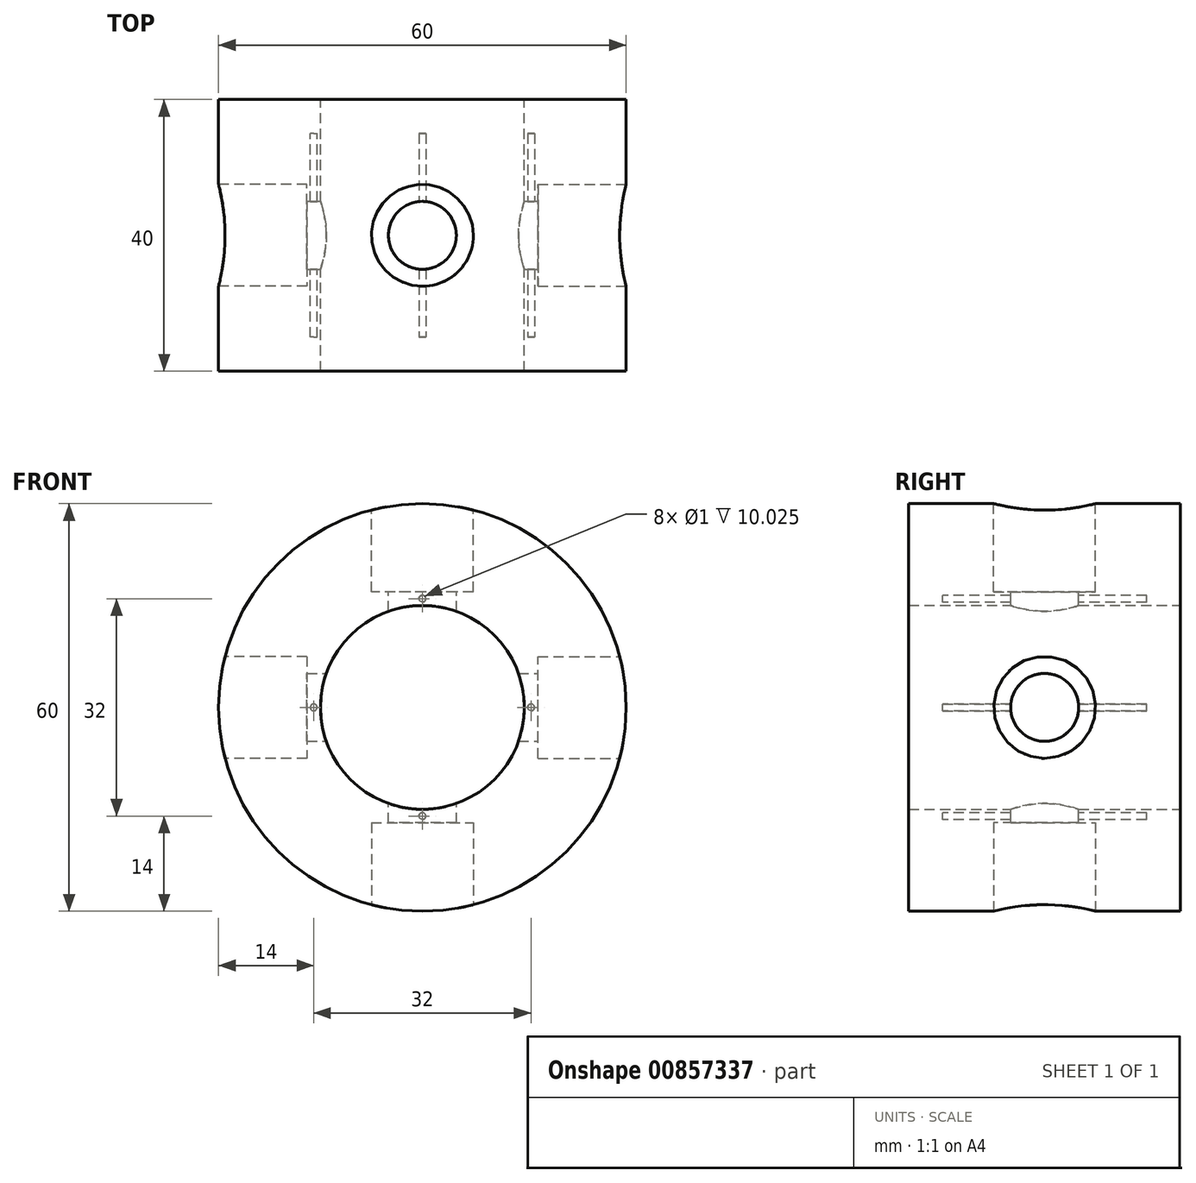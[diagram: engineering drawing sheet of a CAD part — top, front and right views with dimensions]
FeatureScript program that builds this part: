
annotation { "Feature Type Name" : "Feature", "Feature Type Description" : "" }
export const myFeature = defineFeature(function(context is Context, id is Id, definition is map)
    precondition{}
    {
        {
            var Q0;
            Q0=qCreatedBy(makeId("Front.planeOp"),FACE);
            var sketch = newSketch(context, id + "F0", { "sketchPlane" : qUnion([Q0])});
            skCircle(sketch, "E0", {"center": v(0, 0) * mm, "radius": 30 * mm});
            skCircle(sketch, "E1", {"center": v(0, 0) * mm, "radius": 15 * mm});
            skSolve(sketch);
        }
        {
            var Q0;
            Q0=makeQuery(id+"F0.imprint","IMPRINT",FACE,{"disambiguationData":[TD([[makeQuery(id+"F0.imprint","IMPRINT",EDGE,{"derivedFrom":sQuery(id+"F0.wireOp",EDGE,"E0")}),1.0]])]});
            extrude(context, id + "F1", {"entities" : qUnion([Q0]), "endBound" : BoundingType.SYMMETRIC, "depth" : 40 * mm, "offsetDistance" : 25 * mm});
        }
        {
            var Q0;
            Q0=qCreatedBy(makeId("Top.planeOp"),FACE);
            cPlane(context, id + "F2", {"entities" : qUnion([Q0]), "cplaneType" : CPlaneType.OFFSET, "offset" : 30 * mm, "width" : 150 * mm, "height" : 150 * mm});
        }
        {
            var Q0;
            Q0=qCreatedBy(id+"F2.planeOp",FACE);
            var sketch = newSketch(context, id + "F3", { "sketchPlane" : qUnion([Q0])});
            skCircle(sketch, "E2", {"center": v(0, 0) * mm, "radius": 7.5 * mm});
            skSolve(sketch);
        }
        {
            var Q0;
            Q0 = qSketchRegion(id + "F3", true);
            extrude(context, id + "F4", {"entities" : qUnion([Q0]), "operationType" : NewBodyOperationType.REMOVE, "oppositeDirection" : true, "depth" : 13 * mm, "offsetDistance" : 25 * mm});
        }
        {
            var Q0;
            Q0=qCreatedBy(id+"F2.planeOp",FACE);
            var sketch = newSketch(context, id + "F5", { "sketchPlane" : qUnion([Q0])});
            skCircle(sketch, "E3", {"center": v(0, 0) * mm, "radius": 5 * mm});
            skSolve(sketch);
        }
        {
            var Q0;
            Q0 = qSketchRegion(id + "F5", true);
            extrude(context, id + "F6", {"entities" : qUnion([Q0]), "operationType" : NewBodyOperationType.REMOVE, "oppositeDirection" : true, "depth" : 65.5 * mm, "offsetDistance" : 25 * mm});
        }
        {
            var Q0;
            Q0=qCreatedBy(makeId("Top.planeOp"),FACE);
            cPlane(context, id + "F7", {"entities" : qUnion([Q0]), "cplaneType" : CPlaneType.OFFSET, "offset" : 30 * mm, "oppositeDirection" : true, "width" : 150 * mm, "height" : 150 * mm});
        }
        {
            var Q0;
            Q0=qCreatedBy(id+"F7.planeOp",FACE);
            var sketch = newSketch(context, id + "F8", { "sketchPlane" : qUnion([Q0])});
            skCircle(sketch, "E4", {"center": v(0, 0) * mm, "radius": 7.5 * mm});
            skSolve(sketch);
        }
        {
            var Q0;
            Q0 = qSketchRegion(id + "F8", true);
            extrude(context, id + "F9", {"entities" : qUnion([Q0]), "operationType" : NewBodyOperationType.REMOVE, "depth" : 13 * mm, "offsetDistance" : 25 * mm});
        }
        {
            var Q0;
            Q0=qCreatedBy(makeId("Right.planeOp"),FACE);
            cPlane(context, id + "F10", {"entities" : qUnion([Q0]), "cplaneType" : CPlaneType.OFFSET, "offset" : 30 * mm, "width" : 150 * mm, "height" : 150 * mm});
        }
        {
            var Q0;
            Q0=qCreatedBy(makeId("Right.planeOp"),FACE);
            cPlane(context, id + "F11", {"entities" : qUnion([Q0]), "cplaneType" : CPlaneType.OFFSET, "offset" : 30 * mm, "oppositeDirection" : true, "width" : 150 * mm, "height" : 150 * mm});
        }
        {
            var Q0;
            Q0=qCreatedBy(id+"F10.planeOp",FACE);
            var sketch = newSketch(context, id + "F12", { "sketchPlane" : qUnion([Q0])});
            skCircle(sketch, "E5", {"center": v(0, 0) * mm, "radius": 7.5 * mm});
            skSolve(sketch);
        }
        {
            var Q0;
            Q0 = qSketchRegion(id + "F12", true);
            extrude(context, id + "F13", {"entities" : qUnion([Q0]), "operationType" : NewBodyOperationType.REMOVE, "oppositeDirection" : true, "depth" : 13 * mm, "offsetDistance" : 25 * mm});
        }
        {
            var Q0;
            Q0=qCreatedBy(id+"F10.planeOp",FACE);
            var sketch = newSketch(context, id + "F14", { "sketchPlane" : qUnion([Q0])});
            skCircle(sketch, "E6", {"center": v(0, 0) * mm, "radius": 5 * mm});
            skSolve(sketch);
        }
        {
            var Q0;
            Q0 = qSketchRegion(id + "F14", true);
            extrude(context, id + "F15", {"entities" : qUnion([Q0]), "operationType" : NewBodyOperationType.REMOVE, "oppositeDirection" : true, "depth" : 92 * mm, "offsetDistance" : 25 * mm});
        }
        {
            var Q0;
            Q0=qCreatedBy(id+"F11.planeOp",FACE);
            var sketch = newSketch(context, id + "F16", { "sketchPlane" : qUnion([Q0])});
            skCircle(sketch, "E7", {"center": v(0, 0) * mm, "radius": 7.5 * mm});
            skSolve(sketch);
        }
        {
            var Q0;
            Q0 = qSketchRegion(id + "F16", true);
            extrude(context, id + "F17", {"entities" : qUnion([Q0]), "operationType" : NewBodyOperationType.REMOVE, "depth" : 13 * mm, "offsetDistance" : 25 * mm});
        }
        {
            var Q0;
            Q0=qCreatedBy(makeId("Front.planeOp"),FACE);
            var sketch = newSketch(context, id + "F18", { "sketchPlane" : qUnion([Q0])});
            skLineSegment(sketch, "E8", {"start": v(0, 0) * mm, "end": v(0, 16) * mm});
            skCircle(sketch, "E9", {"center": v(0, 16) * mm, "radius": 0.5 * mm});
            skCircle(sketch, "E10.1.0", {"center": v(-16, 0) * mm, "radius": 0.5 * mm});
            skCircle(sketch, "E10.2.0", {"center": v(0, -16) * mm, "radius": 0.5 * mm});
            skCircle(sketch, "E10.3.0", {"center": v(16, 0) * mm, "radius": 0.5 * mm});
            skPoint(sketch, "E10.center", {"position": v(0, 0) * mm});
            skSolve(sketch);
        }
        {
            var Q0;
            Q0=makeQuery(id+"F18.imprint","IMPRINT",FACE,{"disambiguationData":[TD([[makeQuery(id+"F18.imprint","IMPRINT",EDGE,{"derivedFrom":sQuery(id+"F18.wireOp",EDGE,"E9")}),1.0]])]});
            extrude(context, id + "F19", {"entities" : qUnion([Q0]), "operationType" : NewBodyOperationType.REMOVE, "endBound" : BoundingType.SYMMETRIC, "oppositeDirection" : true, "depth" : 30 * mm, "offsetDistance" : 25 * mm});
        }
        {
            var Q0;
            Q0=makeQuery(id+"F18.imprint","IMPRINT",FACE,{"disambiguationData":[TD([[makeQuery(id+"F18.imprint","IMPRINT",EDGE,{"derivedFrom":sQuery(id+"F18.wireOp",EDGE,"E10.3.0")}),1.0]])]});
            extrude(context, id + "F20", {"entities" : qUnion([Q0]), "operationType" : NewBodyOperationType.REMOVE, "endBound" : BoundingType.SYMMETRIC, "oppositeDirection" : true, "depth" : 30 * mm, "offsetDistance" : 25 * mm});
        }
        {
            var Q0;
            Q0=makeQuery(id+"F18.imprint","IMPRINT",FACE,{"disambiguationData":[TD([[makeQuery(id+"F18.imprint","IMPRINT",EDGE,{"derivedFrom":sQuery(id+"F18.wireOp",EDGE,"E10.2.0")}),1.0]])]});
            extrude(context, id + "F21", {"entities" : qUnion([Q0]), "operationType" : NewBodyOperationType.REMOVE, "endBound" : BoundingType.SYMMETRIC, "oppositeDirection" : true, "depth" : 30 * mm, "offsetDistance" : 25 * mm});
        }
        {
            var Q0;
            Q0=makeQuery(id+"F18.imprint","IMPRINT",FACE,{"disambiguationData":[TD([[makeQuery(id+"F18.imprint","IMPRINT",EDGE,{"derivedFrom":sQuery(id+"F18.wireOp",EDGE,"E10.1.0")}),1.0]])]});
            extrude(context, id + "F22", {"entities" : qUnion([Q0]), "operationType" : NewBodyOperationType.REMOVE, "endBound" : BoundingType.SYMMETRIC, "depth" : 30 * mm, "offsetDistance" : 25 * mm});
        }
    });
